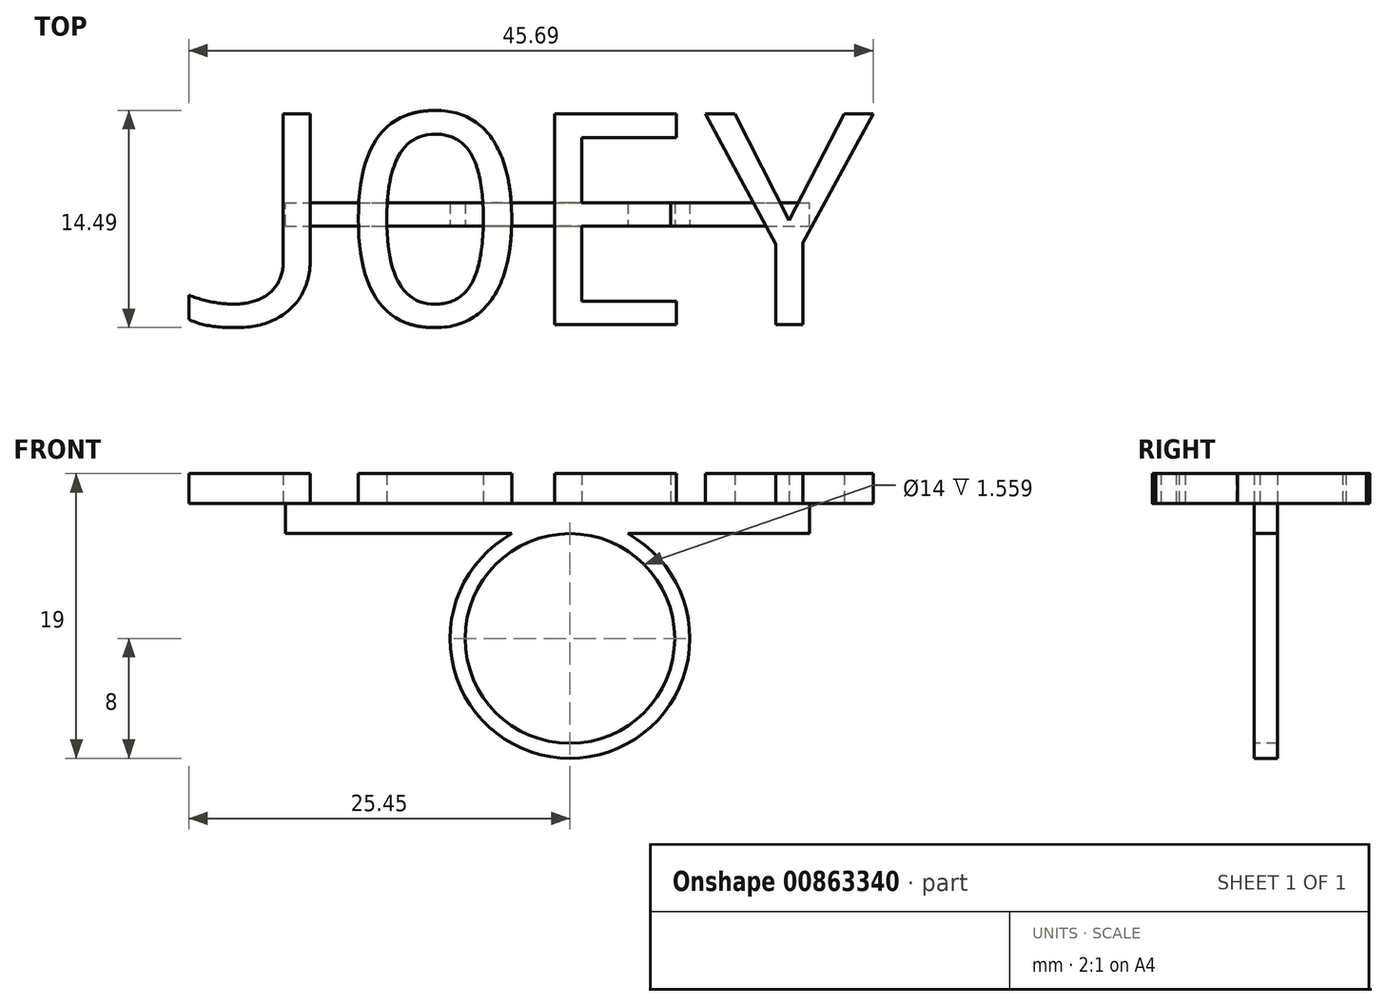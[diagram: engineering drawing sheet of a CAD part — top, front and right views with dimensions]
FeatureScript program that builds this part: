
annotation { "Feature Type Name" : "Feature", "Feature Type Description" : "" }
export const myFeature = defineFeature(function(context is Context, id is Id, definition is map)
    precondition{}
    {
        {
            var Q0;
            Q0=qCreatedBy(makeId("Top.planeOp"),FACE);
            var sketch = newSketch(context, id + "F0", { "sketchPlane" : qUnion([Q0])});
            skText(sketch, "E0", { "text": "JOEY", "fontName": "DroidSansMono.ttf"});
            const initialGuessF0  = {"E0": [0, -0.0142, 1, 0, 0.0142]};
            skSetInitialGuess(sketch, initialGuessF0);
            skSolve(sketch);
        }
        {
            var Q0;
            Q0=makeQuery(id+"F0.imprint","IMPRINT",FACE,{"disambiguationData":[TD([[makeQuery(id+"F0.imprint","IMPRINT",EDGE,{"derivedFrom":sQuery(id+"F0.wireOp",EDGE,"E0.sketch_text.stroke-22")}),-1.0]])]});
            var Q1;
            Q1=makeQuery(id+"F0.imprint","IMPRINT",FACE,{"disambiguationData":[TD([[makeQuery(id+"F0.imprint","IMPRINT",EDGE,{"derivedFrom":sQuery(id+"F0.wireOp",EDGE,"E0.sketch_text.stroke-34")}),-1.0]])]});
            var Q2;
            Q2=makeQuery(id+"F0.imprint","IMPRINT",FACE,{"disambiguationData":[TD([[makeQuery(id+"F0.imprint","IMPRINT",EDGE,{"derivedFrom":sQuery(id+"F0.wireOp",EDGE,"E0.sketch_text.stroke-0")}),-1.0]])]});
            var Q3;
            Q3=makeQuery(id+"F0.imprint","IMPRINT",FACE,{"disambiguationData":[TD([[makeQuery(id+"F0.imprint","IMPRINT",EDGE,{"derivedFrom":sQuery(id+"F0.wireOp",EDGE,"E0.sketch_text.stroke-10")}),-1.0]])]});
            extrude(context, id + "F1", {"entities" : qUnion([Q0, Q1, Q2, Q3]), "depth" : 2 * mm, "offsetDistance" : 25 * mm});
        }
        {
            var Q0;
            Q0=makeQuery(id+"F1.opExtrude","CAP_FACE",FACE,{"disambiguationData":[OSD([sQuery(id+"F0.wireOp",EDGE,"E0.sketch_text.stroke-22"),sQuery(id+"F0.wireOp",EDGE,"E0.sketch_text.stroke-23"),sQuery(id+"F0.wireOp",EDGE,"E0.sketch_text.stroke-24"),sQuery(id+"F0.wireOp",EDGE,"E0.sketch_text.stroke-25"),sQuery(id+"F0.wireOp",EDGE,"E0.sketch_text.stroke-26"),sQuery(id+"F0.wireOp",EDGE,"E0.sketch_text.stroke-27"),sQuery(id+"F0.wireOp",EDGE,"E0.sketch_text.stroke-28"),sQuery(id+"F0.wireOp",EDGE,"E0.sketch_text.stroke-29"),sQuery(id+"F0.wireOp",EDGE,"E0.sketch_text.stroke-30"),sQuery(id+"F0.wireOp",EDGE,"E0.sketch_text.stroke-31"),sQuery(id+"F0.wireOp",EDGE,"E0.sketch_text.stroke-32"),sQuery(id+"F0.wireOp",EDGE,"E0.sketch_text.stroke-33")])],"isStart":true});
            var sketch = newSketch(context, id + "F2", { "sketchPlane" : qUnion([Q0])});
            skLineSegment(sketch, "E1.bottom", {"start": v(33.52, 7.62) * mm, "end": v(7.77, 7.62) * mm});
            skLineSegment(sketch, "E1.top", {"start": v(33.52, 6.06) * mm, "end": v(7.77, 6.06) * mm});
            skLineSegment(sketch, "E1.left", {"start": v(33.52, 7.62) * mm, "end": v(33.52, 6.06) * mm});
            skLineSegment(sketch, "E1.right", {"start": v(7.77, 7.62) * mm, "end": v(7.77, 6.06) * mm});
            skLineSegment(sketch, "E2.bottom", {"start": v(33.52, 7.62) * mm, "end": v(42.77, 7.62) * mm});
            skLineSegment(sketch, "E2.top", {"start": v(33.52, 6.06) * mm, "end": v(42.77, 6.06) * mm});
            skLineSegment(sketch, "E2.right", {"start": v(42.77, 7.62) * mm, "end": v(42.77, 6.06) * mm});
            skSolve(sketch);
        }
        {
            var Q0;
            Q0 = qSketchRegion(id + "F2", true);
            extrude(context, id + "F3", {"entities" : qUnion([Q0]), "depth" : 2 * mm, "offsetDistance" : 25 * mm});
        }
        {
            var Q0;
            Q0=makeQuery(id+"F1.opExtrude","SWEPT_BODY",BODY,{"disambiguationData":[OSD([sQuery(id+"F0.wireOp",EDGE,"E0.sketch_text.stroke-0"),sQuery(id+"F0.wireOp",EDGE,"E0.sketch_text.stroke-1"),sQuery(id+"F0.wireOp",EDGE,"E0.sketch_text.stroke-2"),sQuery(id+"F0.wireOp",EDGE,"E0.sketch_text.stroke-3"),sQuery(id+"F0.wireOp",EDGE,"E0.sketch_text.stroke-4"),sQuery(id+"F0.wireOp",EDGE,"E0.sketch_text.stroke-5"),sQuery(id+"F0.wireOp",EDGE,"E0.sketch_text.stroke-6"),sQuery(id+"F0.wireOp",EDGE,"E0.sketch_text.stroke-7"),sQuery(id+"F0.wireOp",EDGE,"E0.sketch_text.stroke-8"),sQuery(id+"F0.wireOp",EDGE,"E0.sketch_text.stroke-9")])]});
            var Q1;
            Q1=makeQuery(id+"F1.opExtrude","SWEPT_BODY",BODY,{"disambiguationData":[OSD([sQuery(id+"F0.wireOp",EDGE,"E0.sketch_text.stroke-10"),sQuery(id+"F0.wireOp",EDGE,"E0.sketch_text.stroke-11"),sQuery(id+"F0.wireOp",EDGE,"E0.sketch_text.stroke-12"),sQuery(id+"F0.wireOp",EDGE,"E0.sketch_text.stroke-13"),sQuery(id+"F0.wireOp",EDGE,"E0.sketch_text.stroke-14"),sQuery(id+"F0.wireOp",EDGE,"E0.sketch_text.stroke-15"),sQuery(id+"F0.wireOp",EDGE,"E0.sketch_text.stroke-16"),sQuery(id+"F0.wireOp",EDGE,"E0.sketch_text.stroke-17"),sQuery(id+"F0.wireOp",EDGE,"E0.sketch_text.stroke-18"),sQuery(id+"F0.wireOp",EDGE,"E0.sketch_text.stroke-19"),sQuery(id+"F0.wireOp",EDGE,"E0.sketch_text.stroke-20"),sQuery(id+"F0.wireOp",EDGE,"E0.sketch_text.stroke-21")])]});
            var Q2;
            Q2=makeQuery(id+"F1.opExtrude","SWEPT_BODY",BODY,{"disambiguationData":[OSD([sQuery(id+"F0.wireOp",EDGE,"E0.sketch_text.stroke-22"),sQuery(id+"F0.wireOp",EDGE,"E0.sketch_text.stroke-23"),sQuery(id+"F0.wireOp",EDGE,"E0.sketch_text.stroke-24"),sQuery(id+"F0.wireOp",EDGE,"E0.sketch_text.stroke-25"),sQuery(id+"F0.wireOp",EDGE,"E0.sketch_text.stroke-26"),sQuery(id+"F0.wireOp",EDGE,"E0.sketch_text.stroke-27"),sQuery(id+"F0.wireOp",EDGE,"E0.sketch_text.stroke-28"),sQuery(id+"F0.wireOp",EDGE,"E0.sketch_text.stroke-29"),sQuery(id+"F0.wireOp",EDGE,"E0.sketch_text.stroke-30"),sQuery(id+"F0.wireOp",EDGE,"E0.sketch_text.stroke-31"),sQuery(id+"F0.wireOp",EDGE,"E0.sketch_text.stroke-32"),sQuery(id+"F0.wireOp",EDGE,"E0.sketch_text.stroke-33")])]});
            var Q3;
            Q3=makeQuery(id+"F1.opExtrude","SWEPT_BODY",BODY,{"disambiguationData":[OSD([sQuery(id+"F0.wireOp",EDGE,"E0.sketch_text.stroke-34"),sQuery(id+"F0.wireOp",EDGE,"E0.sketch_text.stroke-35"),sQuery(id+"F0.wireOp",EDGE,"E0.sketch_text.stroke-36"),sQuery(id+"F0.wireOp",EDGE,"E0.sketch_text.stroke-37"),sQuery(id+"F0.wireOp",EDGE,"E0.sketch_text.stroke-38"),sQuery(id+"F0.wireOp",EDGE,"E0.sketch_text.stroke-39"),sQuery(id+"F0.wireOp",EDGE,"E0.sketch_text.stroke-40"),sQuery(id+"F0.wireOp",EDGE,"E0.sketch_text.stroke-41"),sQuery(id+"F0.wireOp",EDGE,"E0.sketch_text.stroke-42")])]});
            var Q4;
            Q4=makeQuery(id+"F3.opExtrude","SWEPT_BODY",BODY,{"disambiguationData":[OSD([sQuery(id+"F2.wireOp",EDGE,"E1.bottom"),sQuery(id+"F2.wireOp",EDGE,"E1.top"),sQuery(id+"F2.wireOp",EDGE,"E1.right"),sQuery(id+"F2.wireOp",EDGE,"E2.bottom"),sQuery(id+"F2.wireOp",EDGE,"E2.top"),sQuery(id+"F2.wireOp",EDGE,"E2.right")])]});
            booleanBodies(context, id + "F4", {"operationType" : BooleanOperationType.UNION, "tools" : qUnion([Q0, Q1, Q2, Q3, Q4])});
        }
        {
            var Q0;
            Q0=makeQuery(id+"F4.opBoolean","MERGE",FACE,{"derivedFrom":[makeQuery(id+"F1.opExtrude","SWEPT_FACE",FACE,{"disambiguationData":[OSD([sQuery(id+"F0.wireOp",EDGE,"E0.sketch_text.stroke-30")])]}),makeQuery(id+"F3.opExtrude","SWEPT_FACE",FACE,{"disambiguationData":[OSD([sQuery(id+"F2.wireOp",EDGE,"E1.bottom"),sQuery(id+"F2.wireOp",EDGE,"E2.bottom")])]})]});
            var sketch = newSketch(context, id + "F5", { "sketchPlane" : qUnion([Q0])});
            skCircle(sketch, "E3", {"center": v(26.77, -9) * mm, "radius": 7 * mm});
            skLineSegment(sketch, "E4", {"start": v(42.77, -2) * mm, "end": v(26.77, -2) * mm, "construction": true});
            skCircle(sketch, "E5", {"center": v(26.77, -9) * mm, "radius": 8 * mm});
            skLineSegment(sketch, "E6", {"start": v(26.77, -2) * mm, "end": v(26.77, -9) * mm, "construction": true});
            skSolve(sketch);
        }
        {
            var Q0;
            {var subQ0=sQuery(id+"F5.wireOp",EDGE,"E3");Q0=makeQuery(id+"F5.imprint","IMPRINT",FACE,{"disambiguationData":[TD([[makeQuery(id+"F5.imprint","IMPRINT",EDGE,{"derivedFrom":subQ0}),-1.0]])]});}
            var Q1;
            {var subQ0=sQuery(id+"F5.wireOp",EDGE,"E5");var subQ1=makeQuery(id+"F3.opExtrude","CAP_EDGE",EDGE,{"disambiguationData":[OSD([sQuery(id+"F2.wireOp",EDGE,"E1.bottom"),sQuery(id+"F2.wireOp",EDGE,"E2.bottom")])],"isStart":false});var subQ2=makeQuery(id+"F5.imprint","INTERSECT",VERTEX,{"disambiguationData":[OD(0.0)],"derivedFrom":[subQ1,subQ0]});Q1=makeQuery(id+"F5.imprint","IMPRINT",FACE,{"disambiguationData":[TD([[makeQuery(id+"F5.imprint","IMPRINT",EDGE,{"disambiguationData":[TD([[subQ2,1.0]])],"derivedFrom":subQ0}),1.0]])]});}
            var Q2;
            Q2=makeQuery(id+"F4.opBoolean","MERGE",FACE,{"derivedFrom":[makeQuery(id+"F1.opExtrude","SWEPT_FACE",FACE,{"disambiguationData":[OSD([sQuery(id+"F0.wireOp",EDGE,"E0.sketch_text.stroke-28")])]}),makeQuery(id+"F3.opExtrude","SWEPT_FACE",FACE,{"disambiguationData":[OSD([sQuery(id+"F2.wireOp",EDGE,"E1.top"),sQuery(id+"F2.wireOp",EDGE,"E2.top")])]})]});
            extrude(context, id + "F6", {"entities" : qUnion([Q0, Q1]), "operationType" : NewBodyOperationType.ADD, "endBound" : BoundingType.UP_TO_SURFACE, "oppositeDirection" : true, "depth" : 25 * mm, "endBoundEntityFace" : qUnion([Q2]), "offsetDistance" : 25 * mm});
        }
    });
